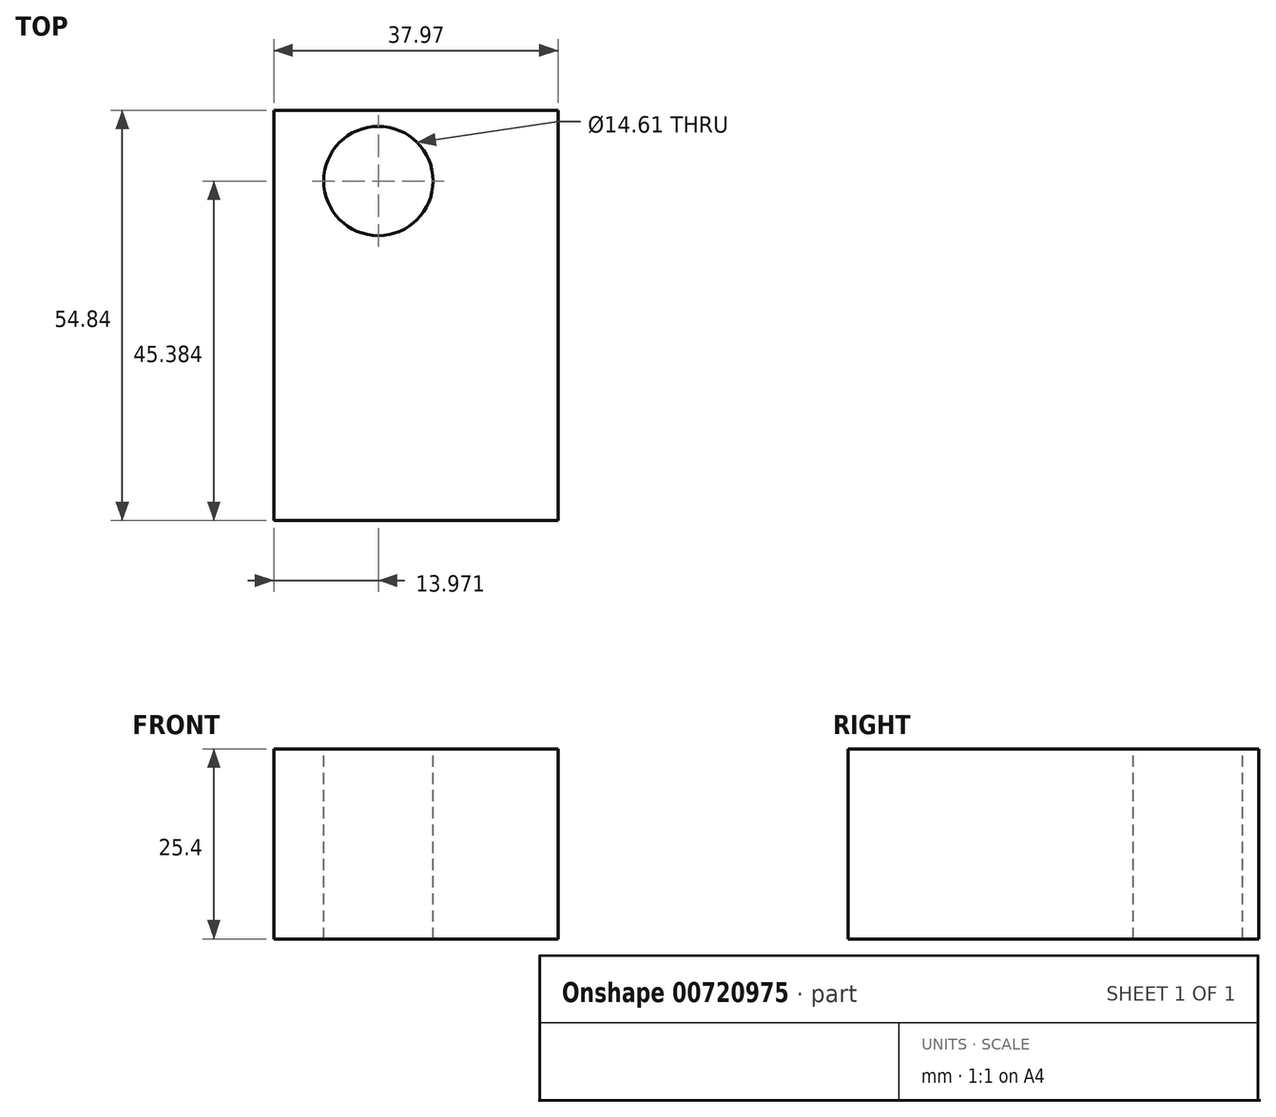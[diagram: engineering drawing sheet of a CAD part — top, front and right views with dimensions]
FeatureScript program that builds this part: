
annotation { "Feature Type Name" : "Feature", "Feature Type Description" : "" }
export const myFeature = defineFeature(function(context is Context, id is Id, definition is map)
    precondition{}
    {
        {
            var Q0;
            Q0=qCreatedBy(makeId("Top.planeOp"),FACE);
            var sketch = newSketch(context, id + "F0", { "sketchPlane" : qUnion([Q0])});
            skLineSegment(sketch, "E0", {"start": v(-37.97, 54.84) * mm, "end": v(-37.97, 0) * mm});
            skLineSegment(sketch, "E1", {"start": v(-37.97, 0) * mm, "end": v(0, 0) * mm});
            skLineSegment(sketch, "E2", {"start": v(0, 0) * mm, "end": v(0, 54.84) * mm});
            skLineSegment(sketch, "E3", {"start": v(0, 54.84) * mm, "end": v(-37.97, 54.84) * mm});
            skSolve(sketch);
        }
        {
            var Q0;
            Q0=makeQuery(id+"F0.imprint","IMPRINT",FACE,{"disambiguationData":[TD([[makeQuery(id+"F0.imprint","IMPRINT",EDGE,{"derivedFrom":sQuery(id+"F0.wireOp",EDGE,"E0")}),1.0]])]});
            extrude(context, id + "F1", {"entities" : qUnion([Q0]), "depth" : 25.4 * mm, "offsetDistance" : 25.4 * mm});
        }
        {
            var Q0;
            Q0=makeQuery(id+"F1.opExtrude","CAP_FACE",FACE,{"disambiguationData":[OSD([sQuery(id+"F0.wireOp",EDGE,"E0"),sQuery(id+"F0.wireOp",EDGE,"E1"),sQuery(id+"F0.wireOp",EDGE,"E2"),sQuery(id+"F0.wireOp",EDGE,"E3")])],"isStart":false});
            var sketch = newSketch(context, id + "F2", { "sketchPlane" : qUnion([Q0])});
            skCircle(sketch, "E4", {"center": v(-24, 45.38) * mm, "radius": 7.3 * mm});
            skSolve(sketch);
        }
        {
            var Q0;
            Q0=makeQuery(id+"F2.imprint","IMPRINT",FACE,{"disambiguationData":[TD([[makeQuery(id+"F2.imprint","IMPRINT",EDGE,{"derivedFrom":sQuery(id+"F2.wireOp",EDGE,"E4")}),1.0]])]});
            extrude(context, id + "F3", {"entities" : qUnion([Q0]), "operationType" : NewBodyOperationType.REMOVE, "oppositeDirection" : true, "depth" : 25.4 * mm, "offsetDistance" : 25.4 * mm});
        }
    });
